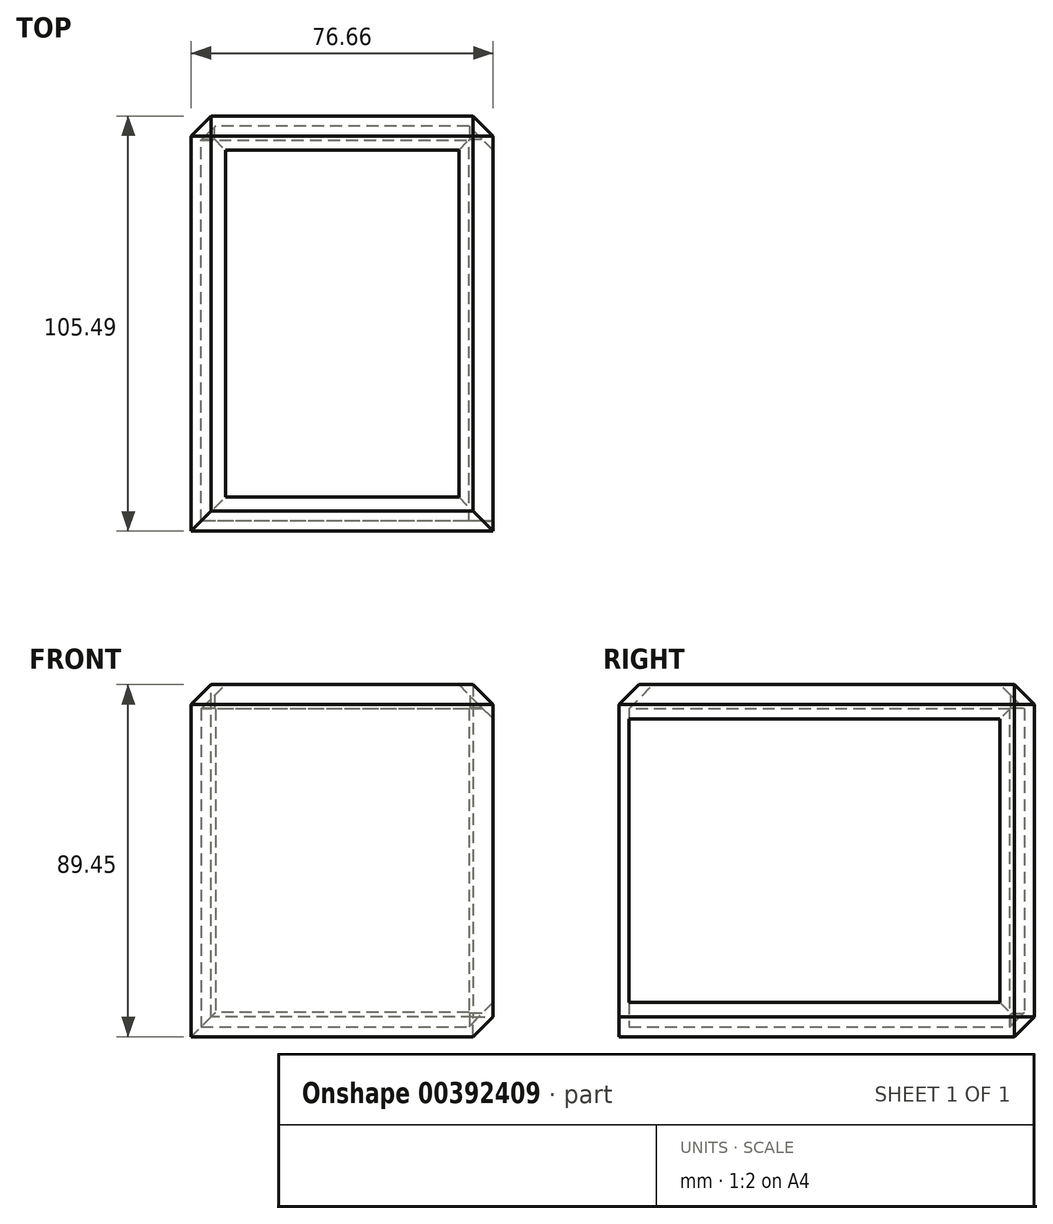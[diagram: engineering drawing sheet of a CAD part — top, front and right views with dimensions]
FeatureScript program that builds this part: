
annotation { "Feature Type Name" : "Feature", "Feature Type Description" : "" }
export const myFeature = defineFeature(function(context is Context, id is Id, definition is map)
    precondition{}
    {
        {
            var Q0;
            Q0=qCreatedBy(makeId("Front.planeOp"),FACE);
            var sketch = newSketch(context, id + "F0", { "sketchPlane" : qUnion([Q0])});
            skLineSegment(sketch, "E0.bottom", {"start": v(28.99, 56.76) * mm, "end": v(-47.67, 56.76) * mm});
            skLineSegment(sketch, "E0.top", {"start": v(28.99, -32.69) * mm, "end": v(-47.67, -32.69) * mm});
            skLineSegment(sketch, "E0.left", {"start": v(28.99, 56.76) * mm, "end": v(28.99, -32.69) * mm});
            skLineSegment(sketch, "E0.right", {"start": v(-47.67, 56.76) * mm, "end": v(-47.67, -32.69) * mm});
            skSolve(sketch);
        }
        {
            var Q0;
            Q0=makeQuery(id+"F0.imprint","IMPRINT",FACE,{"disambiguationData":[TD([[makeQuery(id+"F0.imprint","IMPRINT",EDGE,{"derivedFrom":sQuery(id+"F0.wireOp",EDGE,"E0.bottom")}),1.0]])]});
            var sketch = newSketch(context, id + "F1", { "sketchPlane" : qUnion([Q0])});
            skSolve(sketch);
        }
        {
            var Q0;
            Q0=makeQuery(id+"F1.imprint","IMPRINT",FACE,{"disambiguationData":[TD([[makeQuery(id+"F1.imprint","IMPRINT",EDGE,{"derivedFrom":makeQuery(id+"F0.imprint","IMPRINT",EDGE,{"derivedFrom":sQuery(id+"F0.wireOp",EDGE,"E0.bottom")})}),1.0]])]});
            extrude(context, id + "F2", {"entities" : qUnion([Q0]), "depth" : 105.5 * mm});
        }
        {
            var Q0;
            Q0 = qSketchRegion(id + "F0", true);
            var sketch = newSketch(context, id + "F3", { "sketchPlane" : qUnion([Q0])});
            skCircle(sketch, "E1", {"center": v(-36.4, 0) * mm, "radius": 24.6 * mm});
            skSolve(sketch);
        }
        {
            var Q0;
            Q0=makeQuery(id+"F2.opExtrude","CAP_EDGE",EDGE,{"disambiguationData":[OSD([sQuery(id+"F0.wireOp",EDGE,"E0.bottom")])],"isStart":true});
            var Q1;
            Q1=makeQuery(id+"F2.opExtrude","SWEPT_FACE",FACE,{"disambiguationData":[OSD([sQuery(id+"F0.wireOp",EDGE,"E0.bottom")])]});
            var Q2;
            Q2=makeQuery(id+"F2.opExtrude","CAP_FACE",FACE,{"disambiguationData":[OSD([sQuery(id+"F0.wireOp",EDGE,"E0.bottom"),sQuery(id+"F0.wireOp",EDGE,"E0.top"),sQuery(id+"F0.wireOp",EDGE,"E0.left"),sQuery(id+"F0.wireOp",EDGE,"E0.right")])],"isStart":true});
            var Q3;
            Q3=makeQuery(id+"F2.opExtrude","SWEPT_EDGE",EDGE,{"disambiguationData":[OSD([sQuery(id+"F0.wireOp",EDGE,"E0.top"),sQuery(id+"F0.wireOp",EDGE,"E0.left")])]});
            chamfer(context, id + "F4", {"entities" : qUnion([Q0, Q1, Q2, Q3]), "width" : 5.08 * mm, "tangentPropagation" : true});
        }
        {
            var Q0;
            Q0=makeQuery(id+"F2.opExtrude","SWEPT_FACE",FACE,{"disambiguationData":[OSD([sQuery(id+"F0.wireOp",EDGE,"E0.left")])]});
            var Q1;
            Q1=makeQuery(id+"F2.opExtrude","SWEPT_FACE",FACE,{"disambiguationData":[OSD([sQuery(id+"F0.wireOp",EDGE,"E0.bottom")])]});
            shell(context, id + "F5", {"entities" : qUnion([Q0, Q1]), "thickness" : 2.54 * mm});
        }
    });
